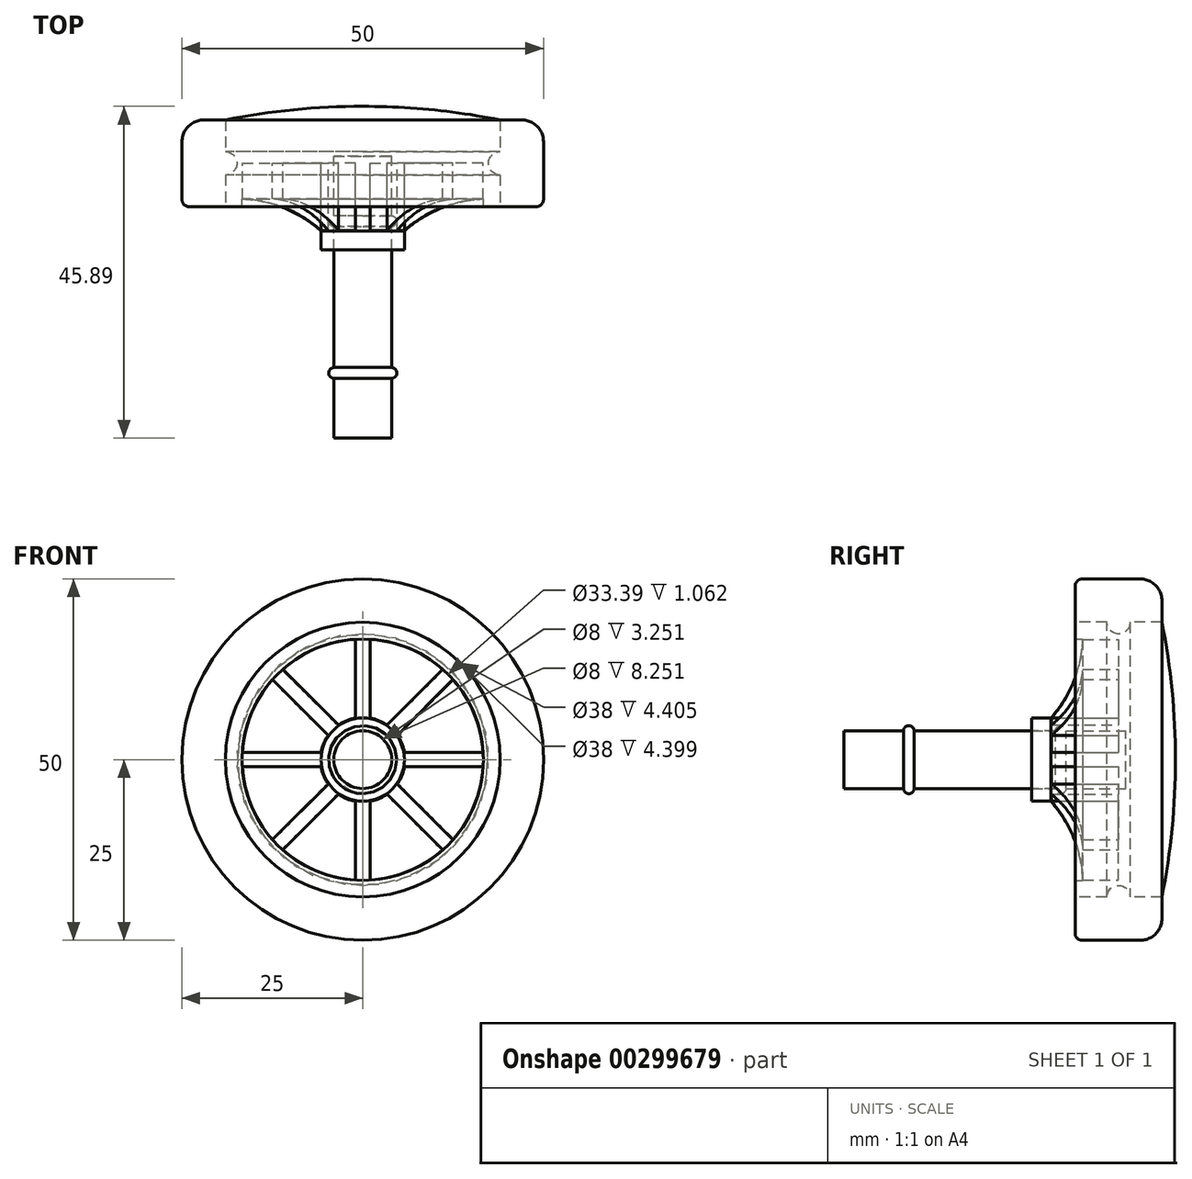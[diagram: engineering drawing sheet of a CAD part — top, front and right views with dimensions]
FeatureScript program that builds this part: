
annotation { "Feature Type Name" : "Feature", "Feature Type Description" : "" }
export const myFeature = defineFeature(function(context is Context, id is Id, definition is map)
    precondition{}
    {
        {
            var Q0;
            Q0=qCreatedBy(makeId("Front.planeOp"),FACE);
            var sketch = newSketch(context, id + "F0", { "sketchPlane" : qUnion([Q0])});
            skCircle(sketch, "E0", {"center": v(0, 0) * mm, "radius": 24.68 * mm});
            skCircle(sketch, "E1", {"center": v(0, 0) * mm, "radius": 19 * mm});
            skCircle(sketch, "E2", {"center": v(0, 0) * mm, "radius": 16.68 * mm});
            skCircle(sketch, "E3", {"center": v(0, 0) * mm, "radius": 5.84 * mm});
            skCircle(sketch, "E4", {"center": v(0, 0) * mm, "radius": 4 * mm});
            skLineSegment(sketch, "E5", {"start": v(16.64, 1) * mm, "end": v(5.76, 1) * mm});
            skLineSegment(sketch, "E6", {"start": v(16.64, -1) * mm, "end": v(5.76, -1) * mm});
            skLineSegment(sketch, "E7.1.0", {"start": v(11.06, 12.48) * mm, "end": v(3.36, 4.78) * mm});
            skLineSegment(sketch, "E7.1.1", {"start": v(12.48, 11.06) * mm, "end": v(4.78, 3.36) * mm});
            skLineSegment(sketch, "E7.2.0", {"start": v(-1, 16.64) * mm, "end": v(-1, 5.76) * mm});
            skLineSegment(sketch, "E7.2.1", {"start": v(1, 16.64) * mm, "end": v(1, 5.76) * mm});
            skLineSegment(sketch, "E7.3.0", {"start": v(-12.48, 11.06) * mm, "end": v(-4.78, 3.36) * mm});
            skLineSegment(sketch, "E7.3.1", {"start": v(-11.06, 12.48) * mm, "end": v(-3.36, 4.78) * mm});
            skLineSegment(sketch, "E7.4.0", {"start": v(-16.64, -1) * mm, "end": v(-5.76, -1) * mm});
            skLineSegment(sketch, "E7.4.1", {"start": v(-16.64, 1) * mm, "end": v(-5.76, 1) * mm});
            skLineSegment(sketch, "E7.5.0", {"start": v(-11.06, -12.48) * mm, "end": v(-3.36, -4.78) * mm});
            skLineSegment(sketch, "E7.5.1", {"start": v(-12.48, -11.06) * mm, "end": v(-4.78, -3.36) * mm});
            skLineSegment(sketch, "E7.6.0", {"start": v(1, -16.64) * mm, "end": v(1, -5.76) * mm});
            skLineSegment(sketch, "E7.6.1", {"start": v(-1, -16.64) * mm, "end": v(-1, -5.76) * mm});
            skLineSegment(sketch, "E7.7.0", {"start": v(12.48, -11.06) * mm, "end": v(4.78, -3.36) * mm});
            skLineSegment(sketch, "E7.7.1", {"start": v(11.06, -12.48) * mm, "end": v(3.36, -4.78) * mm});
            skSolve(sketch);
        }
        {
            var Q0;
            Q0=qCreatedBy(makeId("Front.planeOp"),FACE);
            var sketch = newSketch(context, id + "F1", { "sketchPlane" : qUnion([Q0])});
            skCircle(sketch, "E8.0", {"center": v(0, 0) * mm, "radius": 19 * mm});
            skSolve(sketch);
        }
        {
            var Q0;
            Q0=qSketchRegion(id+"F1",true);
            extrude(context, id + "F2", {"entities" : qUnion([Q0]), "oppositeDirection" : true, "depth" : 6 * mm});
        }
        {
            var Q0;
            Q0=qCreatedBy(makeId("Top.planeOp"),FACE);
            var sketch = newSketch(context, id + "F3", { "sketchPlane" : qUnion([Q0])});
            skLineSegment(sketch, "E9.0", {"start": v(19, 6) * mm, "end": v(0, 6) * mm});
            skArc(sketch, "E10", {"start": v(19, 6) * mm, "mid": v(9.55, 7.41) * mm, "end": v(0, 7.89) * mm});
            skLineSegment(sketch, "E11", {"start": v(0, 0) * mm, "end": v(0, 12.97) * mm, "construction": true});
            skLineSegment(sketch, "E12", {"start": v(0, 6) * mm, "end": v(0, 7.89) * mm});
            skPoint(sketch, "E13.orphan", {"position": v(-19, 6) * mm});
            skSolve(sketch);
        }
        {
            var Q0;
            Q0=qSketchRegion(id+"F3",true);
            var Q1;
            Q1=sQuery(id+"F3.wireOp",EDGE,"E11");
            revolve(context, id + "F4", {"operationType" : NewBodyOperationType.ADD, "entities" : qUnion([Q0]), "axis" : qUnion([Q1]), "revolveType" : RevolveType.FULL});
        }
        {
            var Q0;
            Q0=makeQuery(id+"F0.imprint","IMPRINT",FACE,{"disambiguationData":[TD([[makeQuery(id+"F0.imprint","IMPRINT",EDGE,{"derivedFrom":sQuery(id+"F0.wireOp",EDGE,"E1")}),1.0]])]});
            extrude(context, id + "F5", {"entities" : qUnion([Q0]), "operationType" : NewBodyOperationType.ADD, "depth" : 6 * mm});
        }
        {
            var Q0;
            Q0=makeQuery(id+"F0.imprint","IMPRINT",FACE,{"disambiguationData":[TD([[makeQuery(id+"F0.imprint","IMPRINT",EDGE,{"derivedFrom":sQuery(id+"F0.wireOp",EDGE,"E4")}),-1.0]])]});
            extrude(context, id + "F6", {"entities" : qUnion([Q0]), "operationType" : NewBodyOperationType.ADD, "depth" : 12 * mm});
        }
        {
            var Q0;
            Q0=makeQuery(id+"F0.imprint","IMPRINT",FACE,{"disambiguationData":[TD([[makeQuery(id+"F0.imprint","IMPRINT",EDGE,{"derivedFrom":sQuery(id+"F0.wireOp",EDGE,"E4")}),1.0]])]});
            extrude(context, id + "F7", {"entities" : qUnion([Q0]), "operationType" : NewBodyOperationType.REMOVE, "oppositeDirection" : true, "depth" : 1 * mm});
        }
        {
            var Q0;
            {var subQ0=sQuery(id+"F0.wireOp",EDGE,"E7.3.0");Q0=makeQuery(id+"F0.imprint","IMPRINT",FACE,{"disambiguationData":[TD([[makeQuery(id+"F0.imprint","IMPRINT",EDGE,{"derivedFrom":subQ0}),1.0]])]});}
            var Q1;
            {var subQ0=sQuery(id+"F0.wireOp",EDGE,"E7.2.0");Q1=makeQuery(id+"F0.imprint","IMPRINT",FACE,{"disambiguationData":[TD([[makeQuery(id+"F0.imprint","IMPRINT",EDGE,{"derivedFrom":subQ0}),1.0]])]});}
            var Q2;
            {var subQ0=sQuery(id+"F0.wireOp",EDGE,"E7.1.0");Q2=makeQuery(id+"F0.imprint","IMPRINT",FACE,{"disambiguationData":[TD([[makeQuery(id+"F0.imprint","IMPRINT",EDGE,{"derivedFrom":subQ0}),1.0]])]});}
            var Q3;
            {var subQ0=sQuery(id+"F0.wireOp",EDGE,"E5");Q3=makeQuery(id+"F0.imprint","IMPRINT",FACE,{"disambiguationData":[TD([[makeQuery(id+"F0.imprint","IMPRINT",EDGE,{"derivedFrom":subQ0}),1.0]])]});}
            var Q4;
            {var subQ0=sQuery(id+"F0.wireOp",EDGE,"E7.7.0");Q4=makeQuery(id+"F0.imprint","IMPRINT",FACE,{"disambiguationData":[TD([[makeQuery(id+"F0.imprint","IMPRINT",EDGE,{"derivedFrom":subQ0}),1.0]])]});}
            var Q5;
            {var subQ0=sQuery(id+"F0.wireOp",EDGE,"E7.6.0");Q5=makeQuery(id+"F0.imprint","IMPRINT",FACE,{"disambiguationData":[TD([[makeQuery(id+"F0.imprint","IMPRINT",EDGE,{"derivedFrom":subQ0}),1.0]])]});}
            var Q6;
            {var subQ0=sQuery(id+"F0.wireOp",EDGE,"E7.5.0");Q6=makeQuery(id+"F0.imprint","IMPRINT",FACE,{"disambiguationData":[TD([[makeQuery(id+"F0.imprint","IMPRINT",EDGE,{"derivedFrom":subQ0}),1.0]])]});}
            var Q7;
            {var subQ0=sQuery(id+"F0.wireOp",EDGE,"E7.4.0");Q7=makeQuery(id+"F0.imprint","IMPRINT",FACE,{"disambiguationData":[TD([[makeQuery(id+"F0.imprint","IMPRINT",EDGE,{"derivedFrom":subQ0}),1.0]])]});}
            var Q8;
            Q8=makeQuery(id+"F6.opExtrude","CAP_FACE",FACE,{"disambiguationData":[OSD([sQuery(id+"F0.wireOp",EDGE,"E3"),sQuery(id+"F0.wireOp",EDGE,"E4")])],"isStart":false});
            extrude(context, id + "F8", {"entities" : qUnion([Q0, Q1, Q2, Q3, Q4, Q5, Q6, Q7]), "operationType" : NewBodyOperationType.ADD, "endBound" : BoundingType.UP_TO_SURFACE, "endBoundEntityFace" : qUnion([Q8]), "depth" : 25 * mm});
        }
        {
            var Q0;
            Q0=qCreatedBy(makeId("Right.planeOp"),FACE);
            var sketch = newSketch(context, id + "F9", { "sketchPlane" : qUnion([Q0])});
            skPoint(sketch, "E14.0.end.orphan", {"position": v(0, 19) * mm});
            skPoint(sketch, "E14.0.start.orphan", {"position": v(0, -19) * mm});
            skPoint(sketch, "E15.0", {"position": v(-12, 3.36) * mm});
            skArc(sketch, "E16", {"start": v(-9.36, 5.76) * mm, "mid": v(-6.2, 10.84) * mm, "end": v(-4.94, 16.7) * mm});
            skPoint(sketch, "E16.endSnap0", {"position": v(-7.5, 16.7) * mm});
            skLineSegment(sketch, "E17", {"start": v(-4.94, 16.7) * mm, "end": v(-12.94, 16.7) * mm});
            skLineSegment(sketch, "E18", {"start": v(-12.94, 16.7) * mm, "end": v(-12.94, 5.76) * mm});
            skLineSegment(sketch, "E19.0", {"start": v(-12, 5.76) * mm, "end": v(-9.36, 5.76) * mm});
            skLineSegment(sketch, "E20", {"start": v(-12, 5.76) * mm, "end": v(-12.94, 5.76) * mm});
            skPoint(sketch, "E21.orphan", {"position": v(0, 5.76) * mm});
            skSolve(sketch);
        }
        {
            var Q0;
            Q0=qSketchRegion(id+"F9",true);
            var Q1;
            Q1=sQuery(id+"F3.wireOp",EDGE,"E11");
            revolve(context, id + "F10", {"operationType" : NewBodyOperationType.REMOVE, "entities" : qUnion([Q0]), "axis" : qUnion([Q1]), "revolveType" : RevolveType.FULL, "oppositeDirection" : true});
        }
        {
            var Q0;
            Q0=qCreatedBy(makeId("Right.planeOp"),FACE);
            var sketch = newSketch(context, id + "F11", { "sketchPlane" : qUnion([Q0])});
            skPoint(sketch, "E22.0", {"position": v(0, 19) * mm});
            skArc(sketch, "E23", {"start": v(-1.6, 19) * mm, "mid": v(0, 17.4) * mm, "end": v(1.6, 19) * mm});
            skLineSegment(sketch, "E24", {"start": v(-1.6, 19) * mm, "end": v(1.6, 19) * mm});
            skSolve(sketch);
        }
        {
            var Q0;
            Q0=qSketchRegion(id+"F11",true);
            var Q1;
            Q1=sQuery(id+"F3.wireOp",EDGE,"E11");
            revolve(context, id + "F12", {"operationType" : NewBodyOperationType.REMOVE, "entities" : qUnion([Q0]), "axis" : qUnion([Q1]), "revolveType" : RevolveType.FULL, "oppositeDirection" : true});
        }
        {
            var Q0;
            Q0=qCreatedBy(makeId("Right.planeOp"),FACE);
            var sketch = newSketch(context, id + "F13", { "sketchPlane" : qUnion([Q0])});
            skArc(sketch, "E25", {"start": v(-1.6, 19) * mm, "mid": v(0, 17.4) * mm, "end": v(1.6, 19) * mm});
            skLineSegment(sketch, "E26", {"start": v(1.6, 19) * mm, "end": v(6, 19) * mm});
            skLineSegment(sketch, "E27", {"start": v(-6, 19) * mm, "end": v(-1.6, 19) * mm});
            skLineSegment(sketch, "E28", {"start": v(-6, 19) * mm, "end": v(-6, 25) * mm});
            skLineSegment(sketch, "E29", {"start": v(-6, 25) * mm, "end": v(6, 25) * mm});
            skLineSegment(sketch, "E30", {"start": v(6, 19) * mm, "end": v(6, 25) * mm});
            skLineSegment(sketch, "E31.0", {"start": v(-6, -19) * mm, "end": v(-6, 19) * mm});
            skLineSegment(sketch, "E32", {"start": v(6, -19) * mm, "end": v(1.6, -19) * mm});
            skSolve(sketch);
        }
        {
            var Q0;
            Q0=qSketchRegion(id+"F13",true);
            var Q1;
            Q1=sQuery(id+"F3.wireOp",EDGE,"E11");
            revolve(context, id + "F14", {"entities" : qUnion([Q0]), "axis" : qUnion([Q1]), "revolveType" : RevolveType.FULL});
        }
        {
            var Q0;
            Q0=makeQuery(id+"F14.opRevolve","SWEPT_EDGE",EDGE,{"disambiguationData":[OSD([sQuery(id+"F13.wireOp",EDGE,"E28"),sQuery(id+"F13.wireOp",EDGE,"E29")])]});
            fillet(context, id + "F15", {"entities" : qUnion([Q0]), "radius" : 1 * mm, "tangentPropagation" : true, "allowEdgeOverflow" : false});
        }
        {
            var Q0;
            Q0=makeQuery(id+"F14.opRevolve","SWEPT_EDGE",EDGE,{"disambiguationData":[OSD([sQuery(id+"F13.wireOp",EDGE,"E29"),sQuery(id+"F13.wireOp",EDGE,"E30")])]});
            fillet(context, id + "F16", {"entities" : qUnion([Q0]), "radius" : 3 * mm, "tangentPropagation" : true, "allowEdgeOverflow" : false});
        }
        {
            var Q0;
            Q0=qCreatedBy(makeId("Right.planeOp"),FACE);
            var sketch = newSketch(context, id + "F17", { "sketchPlane" : qUnion([Q0])});
            skLineSegment(sketch, "E33.0", {"start": v(-12, 5.76) * mm, "end": v(-9.36, 5.76) * mm, "construction": true});
            skLineSegment(sketch, "E34", {"start": v(-8.75, 3.96) * mm, "end": v(-7.25, 3.96) * mm});
            skArc(sketch, "E35", {"start": v(-7.25, 3.96) * mm, "mid": v(-8, 4.7) * mm, "end": v(-8.75, 3.96) * mm});
            skPoint(sketch, "E36.orphan", {"position": v(-12, 5.76) * mm});
            skPoint(sketch, "E37.0.start.orphan", {"position": v(-12, -5.76) * mm});
            skPoint(sketch, "E38.orphan", {"position": v(-12, 3.96) * mm});
            skSolve(sketch);
        }
        {
            var Q0;
            Q0=qSketchRegion(id+"F17",true);
            var Q1;
            Q1=sQuery(id+"F3.wireOp",EDGE,"E11");
            revolve(context, id + "F18", {"operationType" : NewBodyOperationType.REMOVE, "entities" : qUnion([Q0]), "axis" : qUnion([Q1]), "revolveType" : RevolveType.FULL, "oppositeDirection" : true});
        }
        {
            var Q0;
            Q0=qCreatedBy(makeId("Right.planeOp"),FACE);
            var sketch = newSketch(context, id + "F19", { "sketchPlane" : qUnion([Q0])});
            skArc(sketch, "E39.0", {"start": v(-7.25, 4) * mm, "mid": v(-8, 4.7) * mm, "end": v(-8.75, 4) * mm});
            skPoint(sketch, "E40.endSnap0", {"position": v(1, 0) * mm});
            skPoint(sketch, "E40.end.orphan", {"position": v(1, 0.1) * mm});
            skLineSegment(sketch, "E41", {"start": v(1, 0) * mm, "end": v(-12, 0) * mm});
            skPoint(sketch, "E42.orphan", {"position": v(1, -4) * mm});
            skLineSegment(sketch, "E43", {"start": v(1, 4) * mm, "end": v(1, 0) * mm});
            skLineSegment(sketch, "E44", {"start": v(-12, 4) * mm, "end": v(-8.75, 4) * mm});
            skPoint(sketch, "E45.orphan", {"position": v(-8.75, 3.96) * mm});
            skPoint(sketch, "E46.orphan", {"position": v(-7.25, 3.96) * mm});
            skLineSegment(sketch, "E47.trimOffspring", {"start": v(-7.25, 4) * mm, "end": v(1, 4) * mm});
            skPoint(sketch, "E48.orphan", {"position": v(-19.03, 4) * mm});
            skPoint(sketch, "E49.orphan", {"position": v(-19, 0) * mm});
            skLineSegment(sketch, "E50.0", {"start": v(-12, 0) * mm, "end": v(-12, 4) * mm, "construction": true});
            skLineSegment(sketch, "E51", {"start": v(-9.36, -5.76) * mm, "end": v(-12, -5.76) * mm});
            skLineSegment(sketch, "E52", {"start": v(-12, 5.76) * mm, "end": v(-9.36, 5.76) * mm});
            skPoint(sketch, "E53.orphan", {"position": v(-12, 5.76) * mm});
            skPoint(sketch, "E54.orphan", {"position": v(-12, -5.76) * mm});
            skLineSegment(sketch, "E55", {"start": v(-12, 4) * mm, "end": v(-18.5, 4) * mm});
            skLineSegment(sketch, "E56", {"start": v(-18.5, 4) * mm, "end": v(-18.5, 0) * mm, "construction": true});
            skLineSegment(sketch, "E57", {"start": v(-18.5, 0) * mm, "end": v(-12, 0) * mm});
            skLineSegment(sketch, "E58.MirrorCS", {"start": v(-25, 4) * mm, "end": v(-18.5, 4) * mm});
            skLineSegment(sketch, "E59.MirrorCS", {"start": v(-25, 4) * mm, "end": v(-28.25, 4) * mm});
            skArc(sketch, "E60.MirrorCS", {"start": v(-29.75, 4) * mm, "mid": v(-29, 4.7) * mm, "end": v(-28.25, 4) * mm});
            skLineSegment(sketch, "E61.MirrorCS", {"start": v(-29.75, 4) * mm, "end": v(-38, 4) * mm});
            skLineSegment(sketch, "E62.MirrorCS", {"start": v(-38, 4) * mm, "end": v(-38, 0) * mm});
            skLineSegment(sketch, "E63.MirrorCS", {"start": v(-38, 0) * mm, "end": v(-25, 0) * mm});
            skLineSegment(sketch, "E64.MirrorCS", {"start": v(-18.5, 0) * mm, "end": v(-25, 0) * mm});
            skSolve(sketch);
        }
        {
            var Q0;
            Q0=qSketchRegion(id+"F19",true);
            var Q1;
            Q1=sQuery(id+"F3.wireOp",EDGE,"E11");
            revolve(context, id + "F20", {"entities" : qUnion([Q0]), "axis" : qUnion([Q1]), "revolveType" : RevolveType.FULL});
        }
    });
